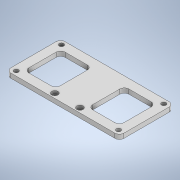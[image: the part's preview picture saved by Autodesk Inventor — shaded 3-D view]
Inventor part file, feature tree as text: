
AUTODESK INVENTOR PART (.ipt)
format: ipt  version: 2021 (Build 250183000, 183)  size: 168,448 bytes
history: native  units: in
note: dims shown in document units (in); Inventor stores cm internally (conversion verified against a paired STEP export)
features: extrude x2, sketch x2, fillet x1
ambient origin geometry x8: Origin, YZ Plane, XZ Plane, XY Plane, X Axis, Y Axis, Z Axis, Center Point
bodies: Solid1 (feature_tree)
feature tree (5):
  extrude  "Extrusion1"  Depth=1.5in
  fillet  "Fillet1"  Radius=0.25in
  extrude  "Extrusion2"  Depth=0.075in
  sketch  "Sketch1"  dims[d0=2.625in d1=1.5in d2=0.25in]
  sketch  "Sketch3"  dims[d3=0.7874in d5=1.25in d6=0.7874in d8=2.825in d11=0.1in d12=0.125in d14=0.125in d15=2.625in d19=0.9in d21=0.125in d22=0.0in d23=0.125in d24=0.125in d25=0.695in d26=0.3475in d27=0.125in d28=0.25in d29=0.25in d30=0.175in d31=0.175in d32=0.075in d33=0.0in]
